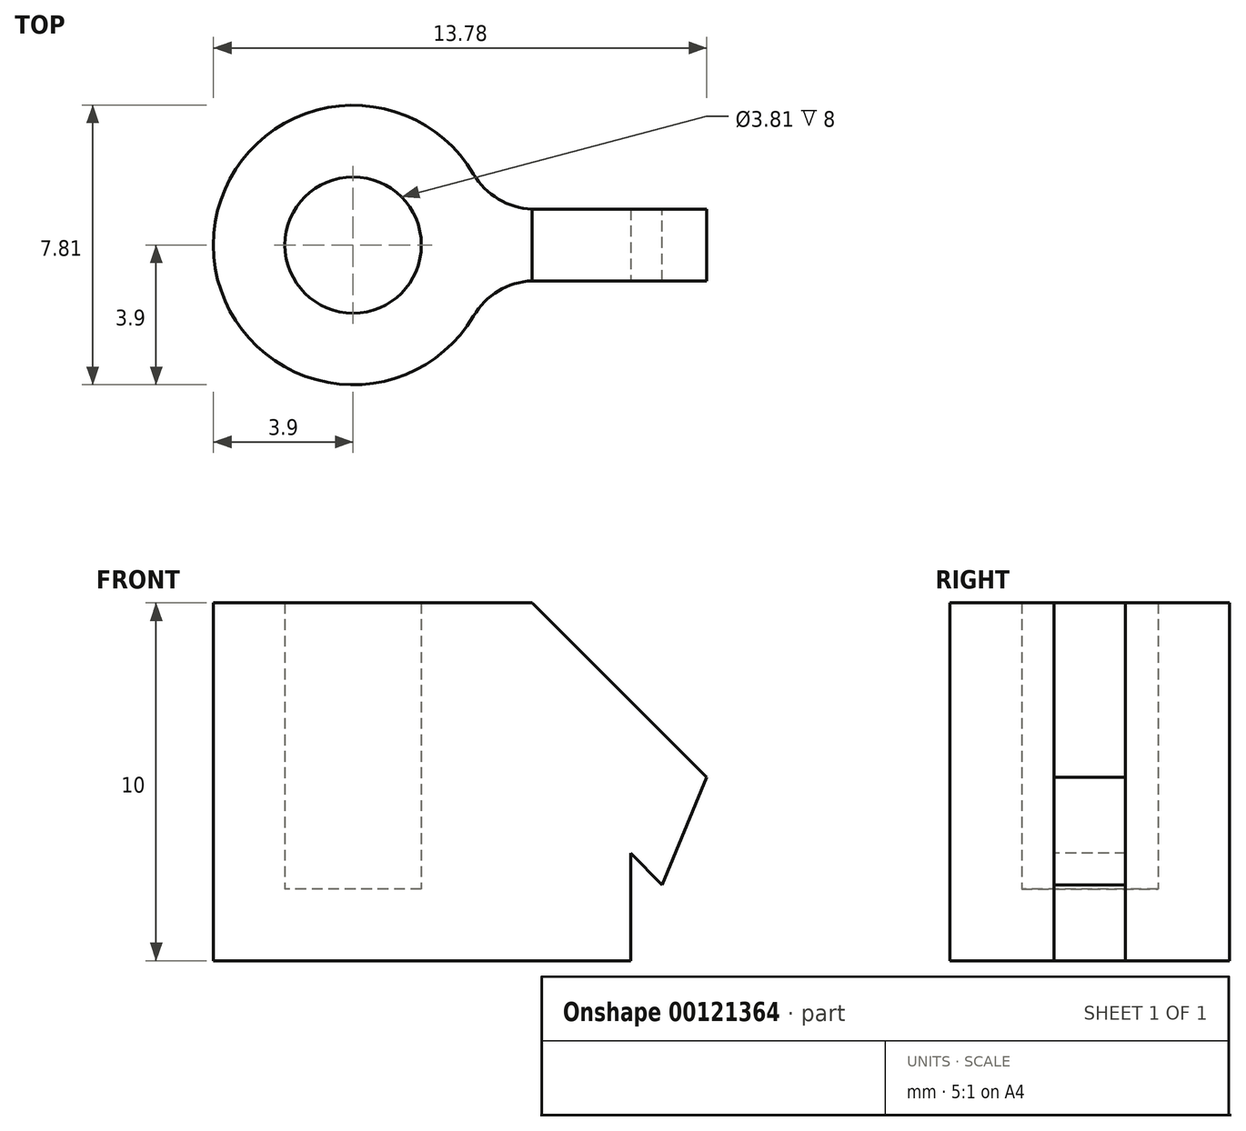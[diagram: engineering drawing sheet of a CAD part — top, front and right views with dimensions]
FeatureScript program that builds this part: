
annotation { "Feature Type Name" : "Feature", "Feature Type Description" : "" }
export const myFeature = defineFeature(function(context is Context, id is Id, definition is map)
    precondition{}
    {
        {
            var Q0;
            Q0=qCreatedBy(makeId("Top.planeOp"),FACE);
            var sketch = newSketch(context, id + "F0", { "sketchPlane" : qUnion([Q0])});
            skCircle(sketch, "E0", {"center": v(0, 0) * mm, "radius": 1.9 * mm});
            skCircle(sketch, "E1.0", {"center": v(0, 0) * mm, "radius": 3.9 * mm});
            skLineSegment(sketch, "E2", {"start": v(0, 0) * mm, "end": v(15, 0) * mm, "construction": true});
            skLineSegment(sketch, "E3", {"start": v(15, 0) * mm, "end": v(15, 1) * mm});
            skLineSegment(sketch, "E4", {"start": v(15, 1) * mm, "end": v(3.77, 1) * mm});
            skLineSegment(sketch, "E5", {"start": v(15, 0) * mm, "end": v(15, -1) * mm});
            skLineSegment(sketch, "E6", {"start": v(15, -1) * mm, "end": v(3.77, -1) * mm});
            skSolve(sketch);
        }
        {
            var Q0;
            Q0 = qSketchRegion(id + "F0", true);
            extrude(context, id + "F1", {"entities" : qUnion([Q0]), "depth" : 10 * mm});
        }
        {
            var Q0;
            Q0=qCreatedBy(makeId("Top.planeOp"),FACE);
            var sketch = newSketch(context, id + "F2", { "sketchPlane" : qUnion([Q0])});
            skCircle(sketch, "E7.0", {"center": v(0, 0) * mm, "radius": 1.9 * mm});
            skSolve(sketch);
        }
        {
            var Q0;
            Q0 = qSketchRegion(id + "F2", true);
            extrude(context, id + "F3", {"entities" : qUnion([Q0]), "operationType" : NewBodyOperationType.ADD, "depth" : 2 * mm});
        }
        {
            var Q0;
            Q0=makeQuery(id+"F1.opExtrude","CAP_EDGE",EDGE,{"disambiguationData":[OSD([sQuery(id+"F0.wireOp",EDGE,"E3"),sQuery(id+"F0.wireOp",EDGE,"E5")])],"isStart":false});
            chamfer(context, id + "F4", {"entities" : qUnion([Q0]), "width" : 10 * mm, "tangentPropagation" : true});
        }
        {
            var Q0;
            Q0=makeQuery(id+"F1.opExtrude","SWEPT_FACE",FACE,{"disambiguationData":[OSD([sQuery(id+"F0.wireOp",EDGE,"E6")])]});
            var sketch = newSketch(context, id + "F5", { "sketchPlane" : qUnion([Q0])});
            skLineSegment(sketch, "E8.0", {"start": v(12.88, -2.12) * mm, "end": v(2.88, 7.88) * mm});
            skLineSegment(sketch, "E9", {"start": v(10.76, 0) * mm, "end": v(7.76, 0) * mm});
            skLineSegment(sketch, "E10", {"start": v(7.76, 0) * mm, "end": v(7.76, 3) * mm});
            skSolve(sketch);
        }
        {
            var Q0;
            Q0 = qSketchRegion(id + "F5", true);
            extrude(context, id + "F6", {"entities" : qUnion([Q0]), "operationType" : NewBodyOperationType.REMOVE, "oppositeDirection" : true, "depth" : 25 * mm});
        }
        {
            var Q0;
            Q0=makeQuery(id+"F1.opExtrude","SWEPT_EDGE",EDGE,{"disambiguationData":[OSD([sQuery(id+"F0.wireOp",EDGE,"E1.0"),sQuery(id+"F0.wireOp",EDGE,"E6")])]});
            var Q1;
            Q1=makeQuery(id+"F1.opExtrude","SWEPT_EDGE",EDGE,{"disambiguationData":[OSD([sQuery(id+"F0.wireOp",EDGE,"E1.0"),sQuery(id+"F0.wireOp",EDGE,"E4")])]});
            fillet(context, id + "F7", {"entities" : qUnion([Q0, Q1]), "radius" : 2 * mm, "tangentPropagation" : true, "allowEdgeOverflow" : false});
        }
        {
            var Q0;
            {var subQ0=sQuery(id+"F0.wireOp",EDGE,"E5");var subQ1=sQuery(id+"F0.wireOp",EDGE,"E3");Q0=makeQuery(id+"F4.opChamfer","BLEND_EDGE",EDGE,{"blendedFrom":[makeQuery(id+"F1.opExtrude","CAP_EDGE",EDGE,{"disambiguationData":[OSD([subQ1,subQ0])],"isStart":false}),makeQuery(id+"F3.boolean.opBoolean","MERGE",FACE,{"derivedFrom":[makeQuery(id+"F1.opExtrude","CAP_FACE",FACE,{"disambiguationData":[OSD([sQuery(id+"F0.wireOp",EDGE,"E0"),sQuery(id+"F0.wireOp",EDGE,"E1.0"),subQ1,sQuery(id+"F0.wireOp",EDGE,"E4"),subQ0,sQuery(id+"F0.wireOp",EDGE,"E6")])],"isStart":true}),makeQuery(id+"F3.opExtrude","CAP_FACE",FACE,{"disambiguationData":[OSD([sQuery(id+"F2.wireOp",EDGE,"E7.0")])],"isStart":true})]})],"blendedInto":[makeQuery(id+"F3.boolean.opBoolean","MERGE",FACE,{"derivedFrom":[makeQuery(id+"F1.opExtrude","CAP_FACE",FACE,{"disambiguationData":[OSD([sQuery(id+"F0.wireOp",EDGE,"E0"),sQuery(id+"F0.wireOp",EDGE,"E1.0"),subQ1,sQuery(id+"F0.wireOp",EDGE,"E4"),subQ0,sQuery(id+"F0.wireOp",EDGE,"E6")])],"isStart":true}),makeQuery(id+"F3.opExtrude","CAP_FACE",FACE,{"disambiguationData":[OSD([sQuery(id+"F2.wireOp",EDGE,"E7.0")])],"isStart":true})]})]});}
            chamfer(context, id + "F8", {"entities" : qUnion([Q0]), "width" : 3 * mm, "tangentPropagation" : true});
        }
    });
